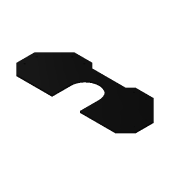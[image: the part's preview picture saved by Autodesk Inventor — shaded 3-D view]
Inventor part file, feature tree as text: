
AUTODESK INVENTOR PART (.ipt)
format: ipt  version: 2014 (Build 180170000, 170)  size: 138,752 bytes
history: native  units: mm
features: extrude x4, sketch x4
ambient origin geometry x8: Origin, YZ Plane, XZ Plane, XY Plane, X Axis, Y Axis, Z Axis, Center Point
bodies: Solid1 (feature_tree)
feature tree (8):
  extrude  "Extrusion1"  Depth=96.0mm
  extrude  "Extrusion2"  Depth=4.0mm
  extrude  "Extrusion3"  Depth=30.0mm
  extrude  "Extrusion4"  Depth=4.0mm
  sketch  "Sketch1"  dims[d0=250.0mm d1=96.0mm]
  sketch  "Sketch2"  dims[d2=4.0mm d3=0.0mm d4=25.0mm]
  sketch  "Sketch3"  dims[d5=45.0mm d6=30.0mm]
  sketch  "Sketch4"  dims[d7=30.0mm d9=7.5mm d10=12.5mm d11=4.0mm d12=30.0mm d13=7.5mm d14=7.5mm d15=7.5mm d16=12.5mm d17=12.5mm d18=4.0mm d19=0.0mm d20=70.0mm d21=4.0mm d22=0.0mm d23=4.0mm d24=0.0mm]
